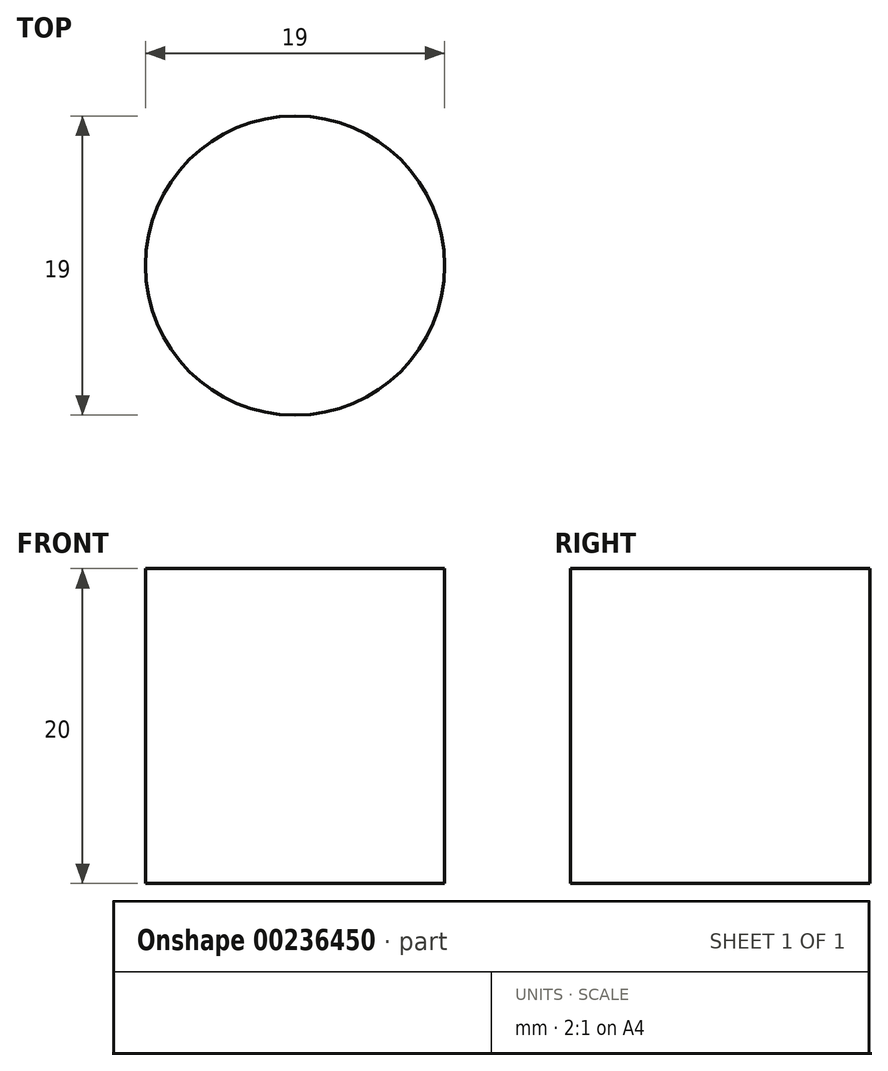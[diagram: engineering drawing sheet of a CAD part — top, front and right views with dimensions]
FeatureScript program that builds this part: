
annotation { "Feature Type Name" : "Feature", "Feature Type Description" : "" }
export const myFeature = defineFeature(function(context is Context, id is Id, definition is map)
    precondition{}
    {
        {
            var Q0;
            Q0=qCreatedBy(makeId("Top.planeOp"),FACE);
            var sketch = newSketch(context, id + "F0", { "sketchPlane" : qUnion([Q0])});
            skCircle(sketch, "E0", {"center": v(0, 0) * mm, "radius": 9.5 * mm});
            skSolve(sketch);
        }
        {
            var Q0;
            Q0=makeQuery(id+"F0.imprint","IMPRINT",FACE,{"disambiguationData":[TD([[makeQuery(id+"F0.imprint","IMPRINT",EDGE,{"derivedFrom":sQuery(id+"F0.wireOp",EDGE,"E0")}),1.0]])]});
            extrude(context, id + "F1", {"entities" : qUnion([Q0]), "depth" : 20 * mm, "offsetDistance" : 25 * mm});
        }
    });
